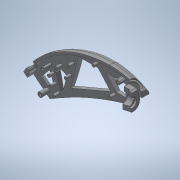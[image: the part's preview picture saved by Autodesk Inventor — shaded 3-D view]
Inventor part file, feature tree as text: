
AUTODESK INVENTOR PART (.ipt)
format: ipt  version: 2020 (Build 240168000, 168)  size: 5,458,944 bytes
history: native  units: in
note: dims shown in document units (in); Inventor stores cm internally (conversion verified against a paired STEP export)
features: extrude x16, sketch x8, other x5, fillet x4, surface_op x2, revolve x2, boolean_combine x1, split x1, chamfer x1, plane x1, delete_face x1, imported_body x1, projected_geometry x1
ambient origin geometry x8: Origin, YZ Plane, XZ Plane, XY Plane, X Axis, Y Axis, Z Axis, Center Point
bodies: Solid1 (feature_tree), Solid196 (feature_tree), Solid197 (feature_tree)
feature tree (44):
  other  "Repaired Geometry1"
  surface_op  "Stitch Surface1"
  sketch  "Sketch2-<F>"  dims[d0=0.03in d1=0.198in]
  extrude  "Extrusion1"  Depth=0.198in
  extrude  "Extrusion2"  Depth=0.184in
  surface_op  "Stitch Surface2"
  boolean_combine  "Combine2"
  split  "Split1"
  extrude  "Extrusion4"  Depth=0.268in
  sketch  "Sketch5-<F>"  dims[d2=0.21in d3=0.184in]
  extrude  "Extrusion5"  Depth=0.4in
  extrude  "Extrusion6"  Depth=0.158in TaperAngle=0.0deg
  extrude  "Extrusion7"  Depth=0.03in
  sketch  "Sketch7-<F>"  dims[d4=0.158in d5=0.0in d7=0.268in]
  extrude  "Extrusion8"  Depth=0.329in
  revolve  "Revolution1"  [1 undecoded]
  revolve  "Revolution2"  [1 undecoded]
  fillet  "Fillet1"  Radius=0.975in
  extrude  "Extrusion9"  Depth=1.086in
  sketch  "Sketch8-<F>"  dims[d8=1.512in d9=0.4in]
  extrude  "Extrusion10"  Depth=0.423in
  extrude  "Extrusion11"  Depth=0.88in
  extrude  "Extrusion12"  Depth=1.0in
  extrude  "Extrusion13"  Depth=1.03in
  chamfer  "Chamfer1"  Distance=1.053in
  extrude  "Extrusion14"  Depth=1.125in
  plane  "Work Plane2"
  extrude  "Extrusion15"  Depth=0.044in
  extrude  "Extrusion16"  Depth=0.09in
  delete_face  "Delete Face2"
  extrude  "Extrusion17"  Depth=0.17in
  fillet  "Fillet3"  Radius=0.24in
  fillet  "Fillet4"  Radius=0.244in
  fillet  "Fillet5"  Radius=0.025in
  other  "Srf3"
  other  "Srf4"
  imported_body  "Base1"
  sketch  "Sketch6-<F>"  dims[d10=0.7in d11=0.158in d12=0.0in]
  sketch  "Sketch9-<F>"  dims[d16=0.004in d17=0.004in d18=0.03in]
  sketch  "Sketch10-<F>"  dims[d19=0.07in]
  projected_geometry  "Projected Loop1"
  sketch  "Sketch11-<F>"  dims[d20=0.031in d45=0.121in d46=0.03in d47=0.158in d48=0.03in d49=0.03in d50=0.03in d51=0.03in d52=0.03in d53=0.03in d54=0.03in d55=0.06in d56=0.03in d57=0.03in d59=0.0962in d60=0.329in d61=0.595in d62=0.85in d63=0.975in d64=1.086in d66=0.423in d67=0.88in d68=1.0in d69=1.03in d70=1.053in d71=1.125in d72=0.044in d73=0.09in d74=0.17in d75=0.24in d76=0.244in d77=0.025in d78=0.016in d79=0.097in d80=0.23in d83=0.225in d84=0.4in d85=0.4055in d86=0.4785in d87=0.4in d88=0.05in d89=1.2in d90=0.0625in d91=0.0in d92=0.2205in d93=0.0206in d94=0.0495in d95=0.0in d96=0.0755in d97=0.0in d124=0.043in d131=0.055in d132=0.11in d133=0.055in d134=0.0235in d135=0.086in d136=0.043in d139=0.045in d141=0.043in d147=0.0235in d148=0.11in d149=0.055in d150=0.2508in d151=0.075in d153=0.0035in d154=0.0035in d155=0.043in d156=0.045in d157=0.055in d158=0.0in d159=90.0deg d160=90.0deg d161=0.04in d162=0.091in d163=0.034in d164=0.064in d165=0.3105in d166=0.025in d167=0.025in d168=0.025in d169=0.025in d170=1.065in d171=1.0in d172=0.0in d173=0.126in d174=0.101in d175=0.108in d176=0.02in d177=0.0in d178=0.009in d179=0.009in d181=1.5748in d183=360.0deg d185=0.012in d186=0.0in d187=0.02in d188=0.0in d189=1.0in d190=0.0in d191=0.02in d192=0.125in d193=0.1374in d194=0.1271in d195=0.159in d196=0.05in d197=0.237in d198=0.317in d199=0.023in d200=1.115in d201=0.2205in d202=0.0in d203=0.07in d204=0.3in d205=-0.1175in d206=0.023in d207=0.0in d208=0.015in d209=0.0in d211=0.03in d212=0.15in d213=0.061in d214=0.0in d216=0.059in d217=0.015in d218=0.004in d219=0.015in d220=0.03in d221=0.059in d222=0.15in d223=0.015in d224=0.275in d225=0.4989in d226=0.014in d227=0.1099in d228=0.015in d229=0.0618in d230=0.014in d231=0.05in]
  other  "OffsetSrf2"
  other  "OffsetSrf1"
note: 2 required parameter values undecoded (feature->parameter linkage not recoverable at this tier; creation-order binding heuristic only, values carry confidence <= 0.55)
